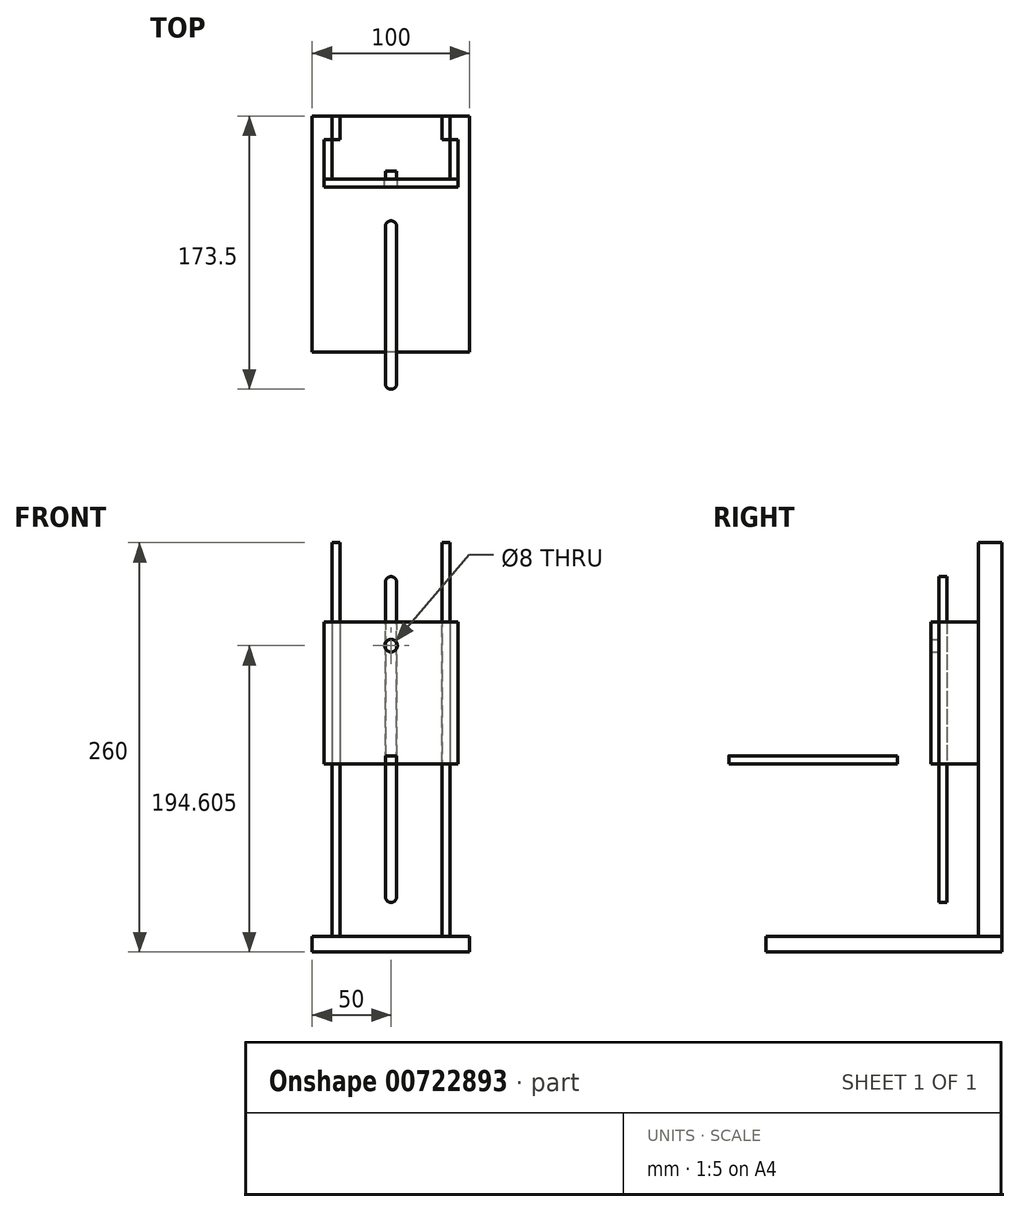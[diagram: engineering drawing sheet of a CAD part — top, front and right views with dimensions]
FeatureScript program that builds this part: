
annotation { "Feature Type Name" : "Feature", "Feature Type Description" : "" }
export const myFeature = defineFeature(function(context is Context, id is Id, definition is map)
    precondition{}
    {
        {
            var Q0;
            Q0=qCreatedBy(makeId("Front.planeOp"),FACE);
            var sketch = newSketch(context, id + "F0", { "sketchPlane" : qUnion([Q0])});
            skLineSegment(sketch, "E0.bottom", {"start": v(50, -5) * mm, "end": v(-50, -5) * mm});
            skLineSegment(sketch, "E0.top", {"start": v(50, 5) * mm, "end": v(-50, 5) * mm});
            skLineSegment(sketch, "E0.left", {"start": v(50, -5) * mm, "end": v(50, 5) * mm});
            skLineSegment(sketch, "E0.right", {"start": v(-50, -5) * mm, "end": v(-50, 5) * mm});
            skPoint(sketch, "E0.middle", {"position": v(0, 0) * mm});
            skSolve(sketch);
        }
        {
            var Q0;
            Q0=makeQuery(id+"F0.imprint","IMPRINT",FACE,{"disambiguationData":[TD([[makeQuery(id+"F0.imprint","IMPRINT",EDGE,{"derivedFrom":sQuery(id+"F0.wireOp",EDGE,"E0.bottom")}),-1.0]])]});
            extrude(context, id + "F1", {"entities" : qUnion([Q0]), "endBound" : BoundingType.SYMMETRIC, "depth" : 150 * mm, "offsetDistance" : 25 * mm});
        }
        {
            var Q0;
            Q0=makeQuery(id+"F1.opExtrude","SWEPT_FACE",FACE,{"disambiguationData":[OSD([sQuery(id+"F0.wireOp",EDGE,"E0.top")])]});
            var sketch = newSketch(context, id + "F2", { "sketchPlane" : qUnion([Q0])});
            skLineSegment(sketch, "E1.bottom", {"start": v(-37.5, 75) * mm, "end": v(-32.5, 75) * mm});
            skLineSegment(sketch, "E2", {"start": v(0, 75) * mm, "end": v(0, 35) * mm, "construction": true});
            skLineSegment(sketch, "E3", {"start": v(0, 35) * mm, "end": v(37.5, 35) * mm});
            skLineSegment(sketch, "E4", {"start": v(37.5, 35) * mm, "end": v(-37.5, 35) * mm});
            skLineSegment(sketch, "E5", {"start": v(-37.5, 35) * mm, "end": v(-37.5, 75) * mm});
            skLineSegment(sketch, "E6", {"start": v(-32.5, 75) * mm, "end": v(-32.5, 40) * mm});
            skLineSegment(sketch, "E7", {"start": v(-32.5, 40) * mm, "end": v(32.5, 40) * mm});
            skLineSegment(sketch, "E8", {"start": v(32.5, 40) * mm, "end": v(32.5, 75) * mm});
            skLineSegment(sketch, "E9", {"start": v(32.5, 75) * mm, "end": v(37.5, 75) * mm});
            skLineSegment(sketch, "E10", {"start": v(37.5, 75) * mm, "end": v(37.5, 35) * mm});
            skSolve(sketch);
        }
        {
            var Q0;
            Q0=qSketchRegion(id+"F2",true);
            extrude(context, id + "F3", {"entities" : qUnion([Q0]), "operationType" : NewBodyOperationType.ADD, "depth" : 250 * mm, "offsetDistance" : 25 * mm});
        }
        {
            var Q0;
            Q0=makeQuery(id+"F3.opExtrude","SWEPT_FACE",FACE,{"disambiguationData":[OSD([sQuery(id+"F2.wireOp",EDGE,"E4")])]});
            var sketch = newSketch(context, id + "F4", { "sketchPlane" : qUnion([Q0])});
            skLineSegment(sketch, "E11.0.0", {"start": v(-37.5, 5) * mm, "end": v(37.5, 5) * mm});
            skLineSegment(sketch, "E11.0.1", {"start": v(37.5, 5) * mm, "end": v(37.5, 255) * mm});
            skLineSegment(sketch, "E11.0.2", {"start": v(37.5, 255) * mm, "end": v(-37.5, 255) * mm});
            skLineSegment(sketch, "E11.0.3", {"start": v(-37.5, 255) * mm, "end": v(-37.5, 5) * mm});
            skLineSegment(sketch, "E12", {"start": v(0, 5) * mm, "end": v(0, 30) * mm});
            skLineSegment(sketch, "E13", {"start": v(0, 30) * mm, "end": v(0, 230) * mm});
            skArc(sketch, "E14.0.startCap", {"start": v(3.5, 30) * mm, "mid": v(0, 26.5) * mm, "end": v(-3.5, 30) * mm});
            skArc(sketch, "E14.0.endCap", {"start": v(-3.5, 230) * mm, "mid": v(0, 233.5) * mm, "end": v(3.5, 230) * mm});
            skLineSegment(sketch, "E14.0.left", {"start": v(-3.5, 30) * mm, "end": v(-3.5, 230) * mm});
            skLineSegment(sketch, "E14.0.right", {"start": v(3.5, 30) * mm, "end": v(3.5, 230) * mm});
            skSolve(sketch);
        }
        {
            var Q0;
            Q0=makeQuery(id+"F4.imprint","IMPRINT",FACE,{"disambiguationData":[TD([[makeQuery(id+"F4.imprint","IMPRINT",EDGE,{"derivedFrom":sQuery(id+"F4.wireOp",EDGE,"E14.0.endCap")}),-1.0]])]});
            extrude(context, id + "F5", {"entities" : qUnion([Q0]), "operationType" : NewBodyOperationType.REMOVE, "oppositeDirection" : true, "depth" : 25 * mm, "offsetDistance" : 25 * mm});
        }
        {
            var Q0;
            Q0=makeQuery(id+"F3.opExtrude","SWEPT_FACE",FACE,{"disambiguationData":[OSD([sQuery(id+"F2.wireOp",EDGE,"E4")])]});
            var sketch = newSketch(context, id + "F6", { "sketchPlane" : qUnion([Q0])});
            skLineSegment(sketch, "E15.0", {"start": v(37.5, 255) * mm, "end": v(37.5, 5) * mm});
            skLineSegment(sketch, "E16.0", {"start": v(-37.5, 255) * mm, "end": v(-37.5, 5) * mm});
            skLineSegment(sketch, "E17", {"start": v(-37.5, 114.6) * mm, "end": v(37.5, 114.6) * mm});
            skLineSegment(sketch, "E18", {"start": v(37.5, 114.6) * mm, "end": v(42.5, 114.6) * mm});
            skLineSegment(sketch, "E19", {"start": v(42.5, 114.6) * mm, "end": v(-42.5, 114.6) * mm});
            skLineSegment(sketch, "E20", {"start": v(-42.5, 114.6) * mm, "end": v(-42.5, 204.6) * mm});
            skLineSegment(sketch, "E21", {"start": v(-42.5, 204.6) * mm, "end": v(42.5, 204.6) * mm});
            skLineSegment(sketch, "E22", {"start": v(42.5, 204.6) * mm, "end": v(42.5, 114.6) * mm});
            skLineSegment(sketch, "E23", {"start": v(0, 204.6) * mm, "end": v(0, 189.6) * mm, "construction": true});
            skCircle(sketch, "E24", {"center": v(0, 189.6) * mm, "radius": 4 * mm});
            skSolve(sketch);
        }
        {
            var Q0;
            Q0 = qSketchRegion(id + "F6", true);
            extrude(context, id + "F7", {"entities" : qUnion([Q0]), "depth" : 5 * mm, "offsetDistance" : 25 * mm});
        }
        {
            var Q0;
            Q0=makeQuery(id+"F7.opExtrude","CAP_FACE",FACE,{"disambiguationData":[OSD([sQuery(id+"F6.wireOp",EDGE,"E19"),sQuery(id+"F6.wireOp",EDGE,"E20"),sQuery(id+"F6.wireOp",EDGE,"E21"),sQuery(id+"F6.wireOp",EDGE,"E22"),sQuery(id+"F6.wireOp",EDGE,"E24")])],"isStart":true});
            var sketch = newSketch(context, id + "F8", { "sketchPlane" : qUnion([Q0])});
            skLineSegment(sketch, "E25.bottom", {"start": v(-42.5, 204.6) * mm, "end": v(-37.5, 204.6) * mm});
            skLineSegment(sketch, "E25.top", {"start": v(-42.5, 114.6) * mm, "end": v(-37.5, 114.6) * mm});
            skLineSegment(sketch, "E25.left", {"start": v(-42.5, 204.6) * mm, "end": v(-42.5, 114.6) * mm});
            skLineSegment(sketch, "E25.right", {"start": v(-37.5, 204.6) * mm, "end": v(-37.5, 114.6) * mm});
            skLineSegment(sketch, "E26.bottom", {"start": v(42.5, 204.6) * mm, "end": v(37.5, 204.6) * mm});
            skLineSegment(sketch, "E26.top", {"start": v(42.5, 114.6) * mm, "end": v(37.5, 114.6) * mm});
            skLineSegment(sketch, "E26.left", {"start": v(42.5, 204.6) * mm, "end": v(42.5, 114.6) * mm});
            skLineSegment(sketch, "E26.right", {"start": v(37.5, 204.6) * mm, "end": v(37.5, 114.6) * mm});
            skSolve(sketch);
        }
        {
            var Q0;
            Q0 = qSketchRegion(id + "F8", true);
            extrude(context, id + "F9", {"entities" : qUnion([Q0]), "depth" : 25 * mm, "offsetDistance" : 25 * mm});
        }
        {
            var Q0;
            Q0=makeQuery(id+"F7.opExtrude","CAP_FACE",FACE,{"disambiguationData":[OSD([sQuery(id+"F6.wireOp",EDGE,"E19"),sQuery(id+"F6.wireOp",EDGE,"E20"),sQuery(id+"F6.wireOp",EDGE,"E21"),sQuery(id+"F6.wireOp",EDGE,"E22"),sQuery(id+"F6.wireOp",EDGE,"E24")])],"isStart":false});
            var sketch = newSketch(context, id + "F10", { "sketchPlane" : qUnion([Q0])});
            skLineSegment(sketch, "E27", {"start": v(0, 114.6) * mm, "end": v(0, 119.6) * mm, "construction": true});
            skLineSegment(sketch, "E28", {"start": v(0, 119.6) * mm, "end": v(-25, 119.6) * mm});
            skLineSegment(sketch, "E29", {"start": v(-25, 119.6) * mm, "end": v(25, 119.6) * mm});
            skLineSegment(sketch, "E30", {"start": v(25, 119.6) * mm, "end": v(25, 114.6) * mm});
            skLineSegment(sketch, "E31", {"start": v(25, 114.6) * mm, "end": v(-25, 114.6) * mm});
            skLineSegment(sketch, "E32", {"start": v(-25, 114.6) * mm, "end": v(-25, 119.6) * mm});
            skSolve(sketch);
        }
        {
            var Q0;
            Q0 = qSketchRegion(id + "F10", true);
            extrude(context, id + "F11", {"entities" : qUnion([Q0]), "operationType" : NewBodyOperationType.ADD, "depth" : 150 * mm, "offsetDistance" : 25 * mm});
        }
        {
            var Q0;
            Q0=makeQuery(id+"F11.opExtrude","SWEPT_FACE",FACE,{"disambiguationData":[OSD([sQuery(id+"F10.wireOp",EDGE,"E29")])]});
            var sketch = newSketch(context, id + "F12", { "sketchPlane" : qUnion([Q0])});
            skLineSegment(sketch, "E33.0.0", {"start": v(25, 30) * mm, "end": v(-25, 30) * mm});
            skLineSegment(sketch, "E33.0.1", {"start": v(-25, 30) * mm, "end": v(-25, -120) * mm});
            skLineSegment(sketch, "E33.0.2", {"start": v(-25, -120) * mm, "end": v(25, -120) * mm});
            skLineSegment(sketch, "E33.0.3", {"start": v(25, -120) * mm, "end": v(25, 30) * mm});
            skLineSegment(sketch, "E34", {"start": v(0, -120) * mm, "end": v(0, -95) * mm, "construction": true});
            skLineSegment(sketch, "E35", {"start": v(0, -95) * mm, "end": v(0, 5) * mm, "construction": true});
            skArc(sketch, "E36.0.startCap", {"start": v(3.5, -95) * mm, "mid": v(0, -98.5) * mm, "end": v(-3.5, -95) * mm});
            skArc(sketch, "E36.0.endCap", {"start": v(-3.5, 5) * mm, "mid": v(0, 8.5) * mm, "end": v(3.5, 5) * mm});
            skLineSegment(sketch, "E36.0.left", {"start": v(-3.5, -95) * mm, "end": v(-3.5, 5) * mm});
            skLineSegment(sketch, "E36.0.right", {"start": v(3.5, -95) * mm, "end": v(3.5, 5) * mm});
            skSolve(sketch);
        }
        {
            var Q0;
            Q0=makeQuery(id+"F12.imprint","IMPRINT",FACE,{"disambiguationData":[TD([[makeQuery(id+"F12.imprint","IMPRINT",EDGE,{"derivedFrom":sQuery(id+"F12.wireOp",EDGE,"E36.0.startCap")}),-1.0]])]});
            extrude(context, id + "F13", {"entities" : qUnion([Q0]), "operationType" : NewBodyOperationType.REMOVE, "oppositeDirection" : true, "depth" : 25 * mm, "offsetDistance" : 25 * mm});
        }
    });
